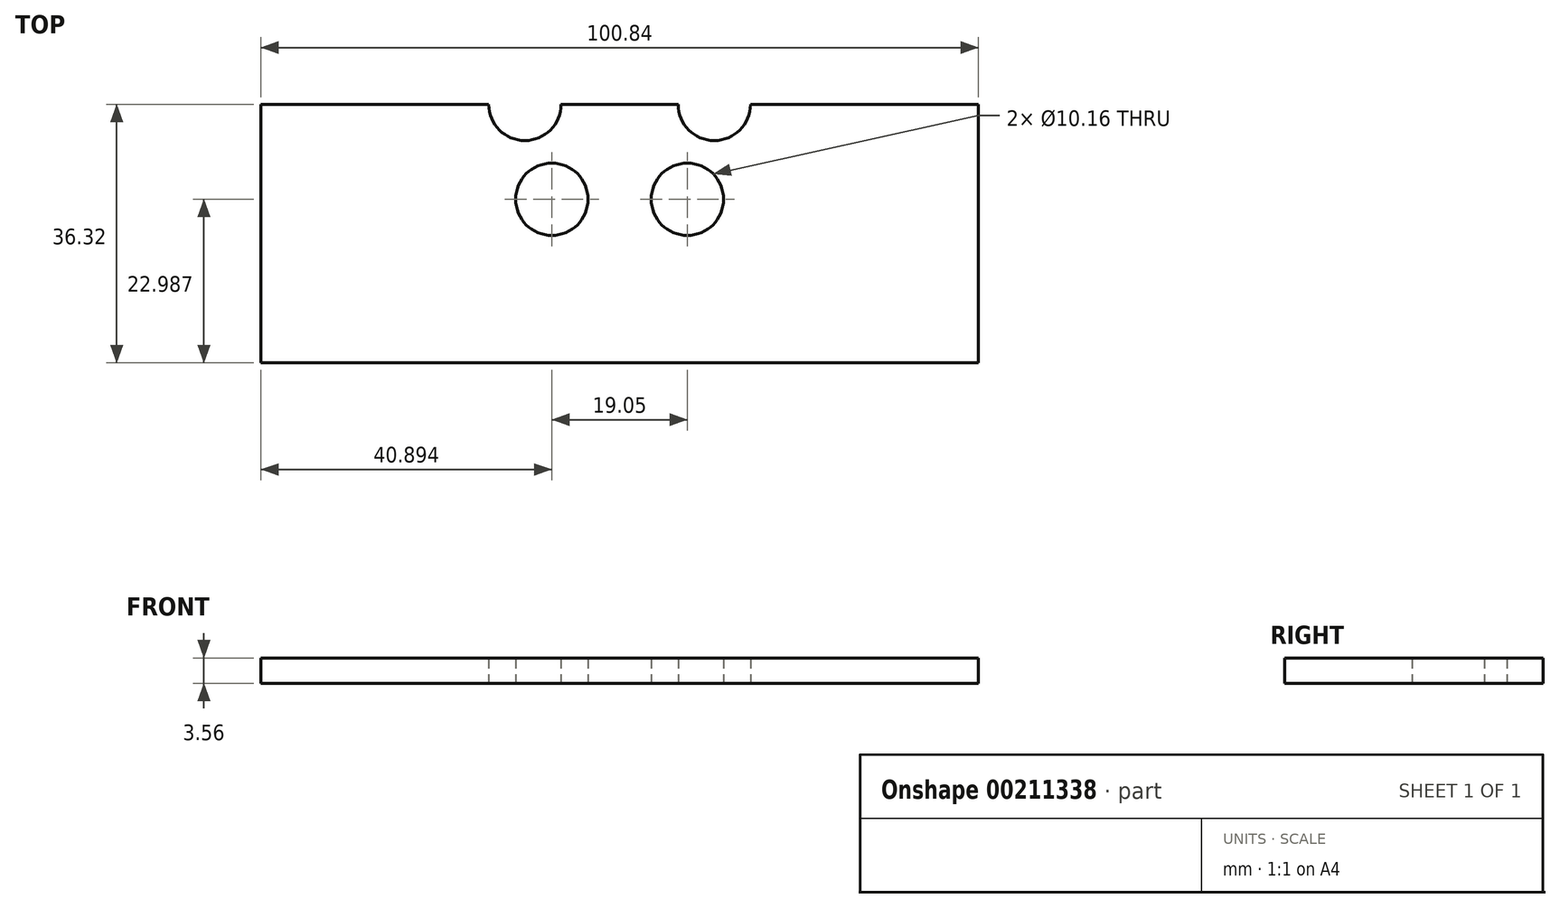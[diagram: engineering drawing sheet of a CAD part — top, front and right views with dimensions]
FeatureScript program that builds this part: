
annotation { "Feature Type Name" : "Feature", "Feature Type Description" : "" }
export const myFeature = defineFeature(function(context is Context, id is Id, definition is map)
    precondition{}
    {
        {
            var Q0;
            Q0=qCreatedBy(makeId("Top.planeOp"),FACE);
            var sketch = newSketch(context, id + "F0", { "sketchPlane" : qUnion([Q0])});
            skLineSegment(sketch, "E0.bottom", {"start": v(0, 0) * mm, "end": v(100.84, 0) * mm});
            skLineSegment(sketch, "E0.top", {"start": v(0, 36.32) * mm, "end": v(32.03, 36.32) * mm});
            skLineSegment(sketch, "E0.left", {"start": v(0, 0) * mm, "end": v(0, 36.32) * mm});
            skLineSegment(sketch, "E0.right", {"start": v(100.84, 0) * mm, "end": v(100.84, 36.32) * mm});
            skArc(sketch, "E1", {"start": v(32.03, 36.32) * mm, "mid": v(37.1, 31.24) * mm, "end": v(42.19, 36.32) * mm});
            skLineSegment(sketch, "E2", {"start": v(50.42, 36.32) * mm, "end": v(50.42, 0) * mm, "construction": true});
            skArc(sketch, "E3.MirrorC", {"start": v(68.8, 36.32) * mm, "mid": v(63.73, 31.24) * mm, "end": v(58.65, 36.32) * mm});
            skCircle(sketch, "E4", {"center": v(40.9, 22.99) * mm, "radius": 5.08 * mm});
            skCircle(sketch, "E5.MirrorC", {"center": v(59.94, 22.99) * mm, "radius": 5.08 * mm});
            skLineSegment(sketch, "E6.trimOffspring", {"start": v(42.19, 36.32) * mm, "end": v(58.65, 36.32) * mm});
            skLineSegment(sketch, "E7.trimOffspring", {"start": v(68.8, 36.32) * mm, "end": v(100.84, 36.32) * mm});
            skSolve(sketch);
        }
        {
            var Q0;
            Q0 = qSketchRegion(id + "F0", true);
            extrude(context, id + "F1", {"entities" : qUnion([Q0]), "depth" : 3.56 * mm});
        }
    });
